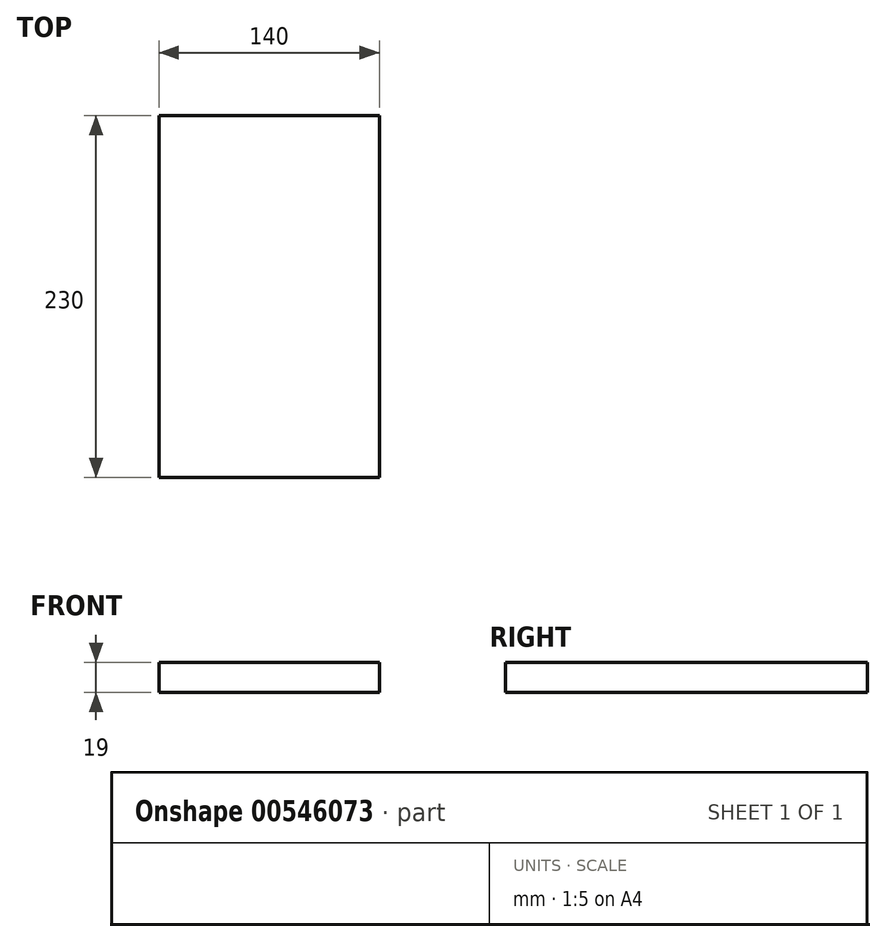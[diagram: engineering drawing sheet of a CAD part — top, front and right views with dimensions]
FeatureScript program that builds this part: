
annotation { "Feature Type Name" : "Feature", "Feature Type Description" : "" }
export const myFeature = defineFeature(function(context is Context, id is Id, definition is map)
    precondition{}
    {
        {
            var Q0;
            Q0=qCreatedBy(makeId("Top.planeOp"),FACE);
            var sketch = newSketch(context, id + "F0", { "sketchPlane" : qUnion([Q0])});
            skLineSegment(sketch, "E0.bottom", {"start": v(-70, 115) * mm, "end": v(70, 115) * mm});
            skLineSegment(sketch, "E0.top", {"start": v(-70, -115) * mm, "end": v(70, -115) * mm});
            skLineSegment(sketch, "E0.left", {"start": v(-70, 115) * mm, "end": v(-70, -115) * mm});
            skLineSegment(sketch, "E0.right", {"start": v(70, 115) * mm, "end": v(70, -115) * mm});
            skPoint(sketch, "E0.middle", {"position": v(0, 0) * mm});
            skSolve(sketch);
        }
        {
            var Q0;
            Q0 = qSketchRegion(id + "F0", true);
            extrude(context, id + "F1", {"entities" : qUnion([Q0]), "depth" : 19 * mm, "offsetDistance" : 25 * mm});
        }
    });
